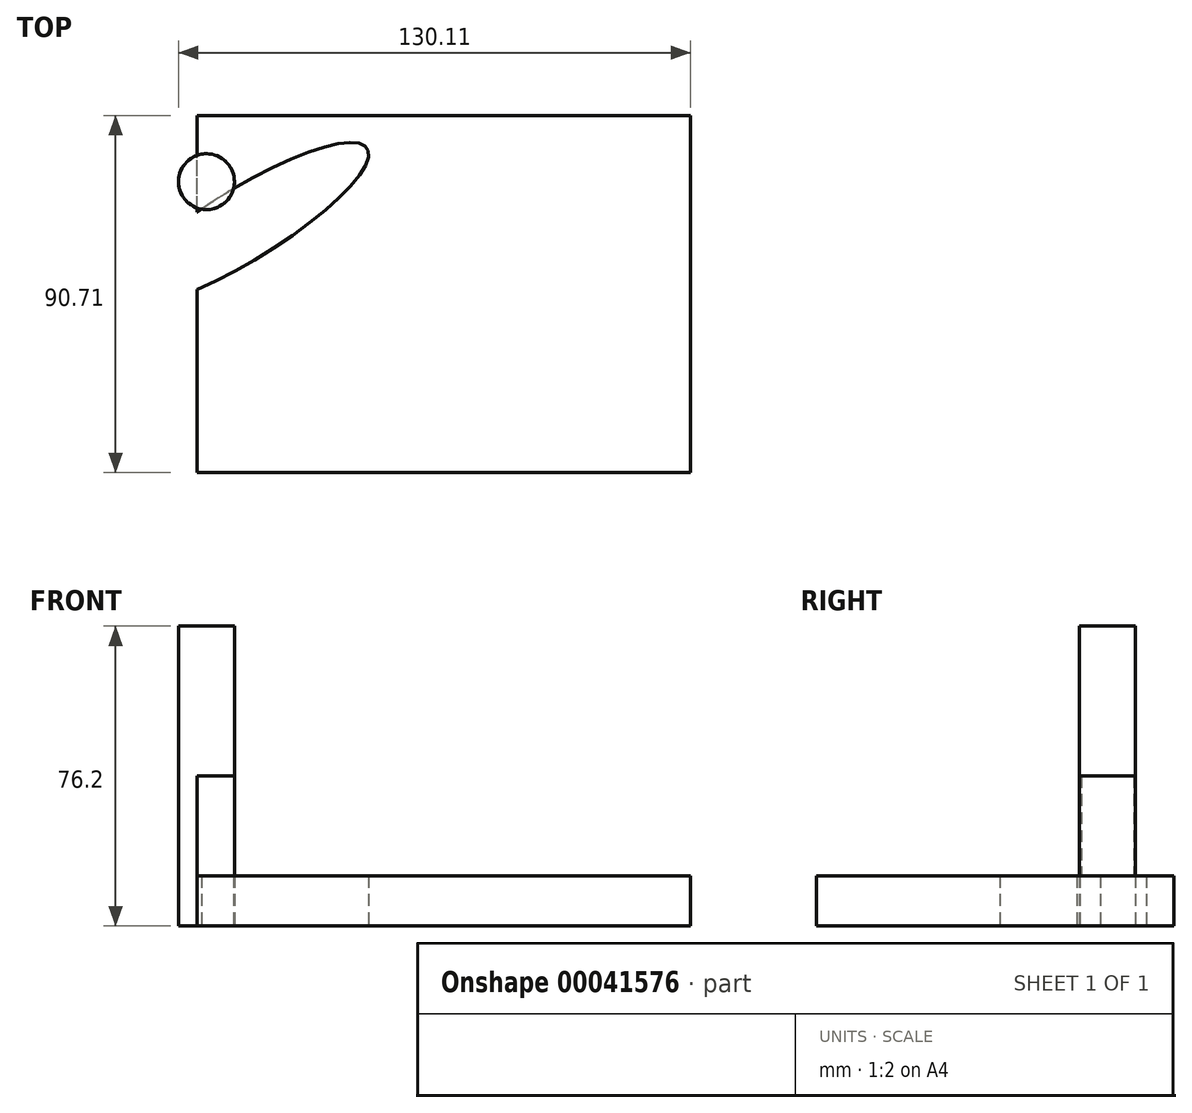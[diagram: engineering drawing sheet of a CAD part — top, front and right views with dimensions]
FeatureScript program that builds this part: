
annotation { "Feature Type Name" : "Feature", "Feature Type Description" : "" }
export const myFeature = defineFeature(function(context is Context, id is Id, definition is map)
    precondition{}
    {
        {
            var Q0;
            Q0=qCreatedBy(makeId("Top.planeOp"),FACE);
            var sketch = newSketch(context, id + "F5", { "sketchPlane" : qUnion([Q0])});
            skLineSegment(sketch, "E0.bottom", {"start": v(35.04, 0) * mm, "end": v(-90.35, 0) * mm});
            skLineSegment(sketch, "E0.top", {"start": v(35.04, 90.71) * mm, "end": v(-90.35, 90.71) * mm});
            skLineSegment(sketch, "E0.left", {"start": v(35.04, 0) * mm, "end": v(35.04, 90.71) * mm});
            skLineSegment(sketch, "E0.right", {"start": v(-90.35, 0) * mm, "end": v(-90.35, 90.71) * mm});
            skSolve(sketch);
        }
        {
            var Q0;
            Q0=makeQuery(id+"F5.imprint","IMPRINT",FACE,{"disambiguationData":[TD([[makeQuery(id+"F5.imprint","IMPRINT",EDGE,{"derivedFrom":sQuery(id+"F5.wireOp",EDGE,"E0.bottom")}),-1.0]])]});
            extrude(context, id + "F0", {"entities" : qUnion([Q0]), "depth" : 25.4 * mm});
        }
        {
            var Q0;
            Q0=qCreatedBy(makeId("Top.planeOp"),FACE);
            var sketch = newSketch(context, id + "F1", { "sketchPlane" : qUnion([Q0])});
            skEllipse(sketch, "E1", {"center": v(-78.32, 63.13) * mm, "majorRadius": 36.62 * mm, "minorRadius": 9.13 * mm, "majorAxis": v(0.85, 0.52)});
            skSolve(sketch);
        }
        {
            var Q0;
            Q0 = qSketchRegion(id + "F1", true);
            var Q1;
            Q1=makeQuery(id+"F0.opExtrude","CAP_FACE",FACE,{"disambiguationData":[OSD([sQuery(id+"F5.wireOp",EDGE,"E0.bottom"),sQuery(id+"F5.wireOp",EDGE,"E0.top"),sQuery(id+"F5.wireOp",EDGE,"E0.left"),sQuery(id+"F5.wireOp",EDGE,"E0.right")])],"isStart":false});
            extrude(context, id + "F2", {"entities" : qUnion([Q0, Q1]), "operationType" : NewBodyOperationType.REMOVE, "depth" : 25.4 * mm, "symmetric" : true});
        }
        {
            var Q0;
            Q0=qCreatedBy(makeId("Top.planeOp"),FACE);
            var sketch = newSketch(context, id + "F3", { "sketchPlane" : qUnion([Q0])});
            skCircle(sketch, "E2", {"center": v(-87.97, 73.9) * mm, "radius": 7.1 * mm});
            skSolve(sketch);
        }
        {
            var Q0;
            Q0 = qSketchRegion(id + "F3", true);
            extrude(context, id + "F4", {"entities" : qUnion([Q0]), "depth" : 76.2 * mm});
        }
    });
